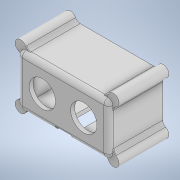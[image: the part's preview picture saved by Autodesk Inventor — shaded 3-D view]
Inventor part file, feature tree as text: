
AUTODESK INVENTOR PART (.ipt)
format: ipt  version: 2020 (Build 240168000, 168)  size: 390,144 bytes
history: native  units: in
note: dims shown in document units (in); Inventor stores cm internally (conversion verified against a paired STEP export)
features: extrude x7, sketch x6, fillet x2, plane x2, mirror x2, projected_geometry x2
ambient origin geometry x8: Origin, YZ Plane, XZ Plane, XY Plane, X Axis, Y Axis, Z Axis, Center Point
bodies: Solid1 (feature_tree)
feature tree (21):
  extrude  "Extrusion1"  Depth=0.66in
  sketch  "Sketch3"  dims[d2=0.38in d4=0.85in]
  extrude  "Extrusion2"  Depth=0.85in
  extrude  "Extrusion3"  Depth=0.41in
  fillet  "Fillet1"  Radius=0.41in
  extrude  "Extrusion4"  Depth=0.1in
  extrude  "Extrusion5"  Depth=1.25in TaperAngle=0.0deg
  extrude  "Extrusion6"  Depth=0.125in
  extrude  "Extrusion7"  Depth=0.125in
  plane  "Work Plane1"
  plane  "Work Plane2"
  mirror  "Mirror1"
  mirror  "Mirror2"
  fillet  "Fillet2"  Radius=1.09in
  sketch  "Sketch2"  dims[d0=0.66in d1=0.66in]
  projected_geometry  "Projected Loop1"
  sketch  "Sketch4"  dims[d5=0.43in d6=0.41in d7=0.41in]
  sketch  "Sketch5"  dims[d8=0.1in d9=0.0in d11=0.1in]
  projected_geometry  "Projected Loop2"
  sketch  "Sketch6"  dims[d12=0.12in d13=1.25in d14=0.0in]
  sketch  "Sketch7"  dims[d15=1.25in d16=0.0in d17=0.125in d18=0.6in d19=1.09in d20=0.0in d21=0.597in d22=0.0in d23=0.1094in d24=0.14in d25=1.25in d26=0.0in d27=0.05in d28=0.0in d29=0.125in d30=0.4in]
